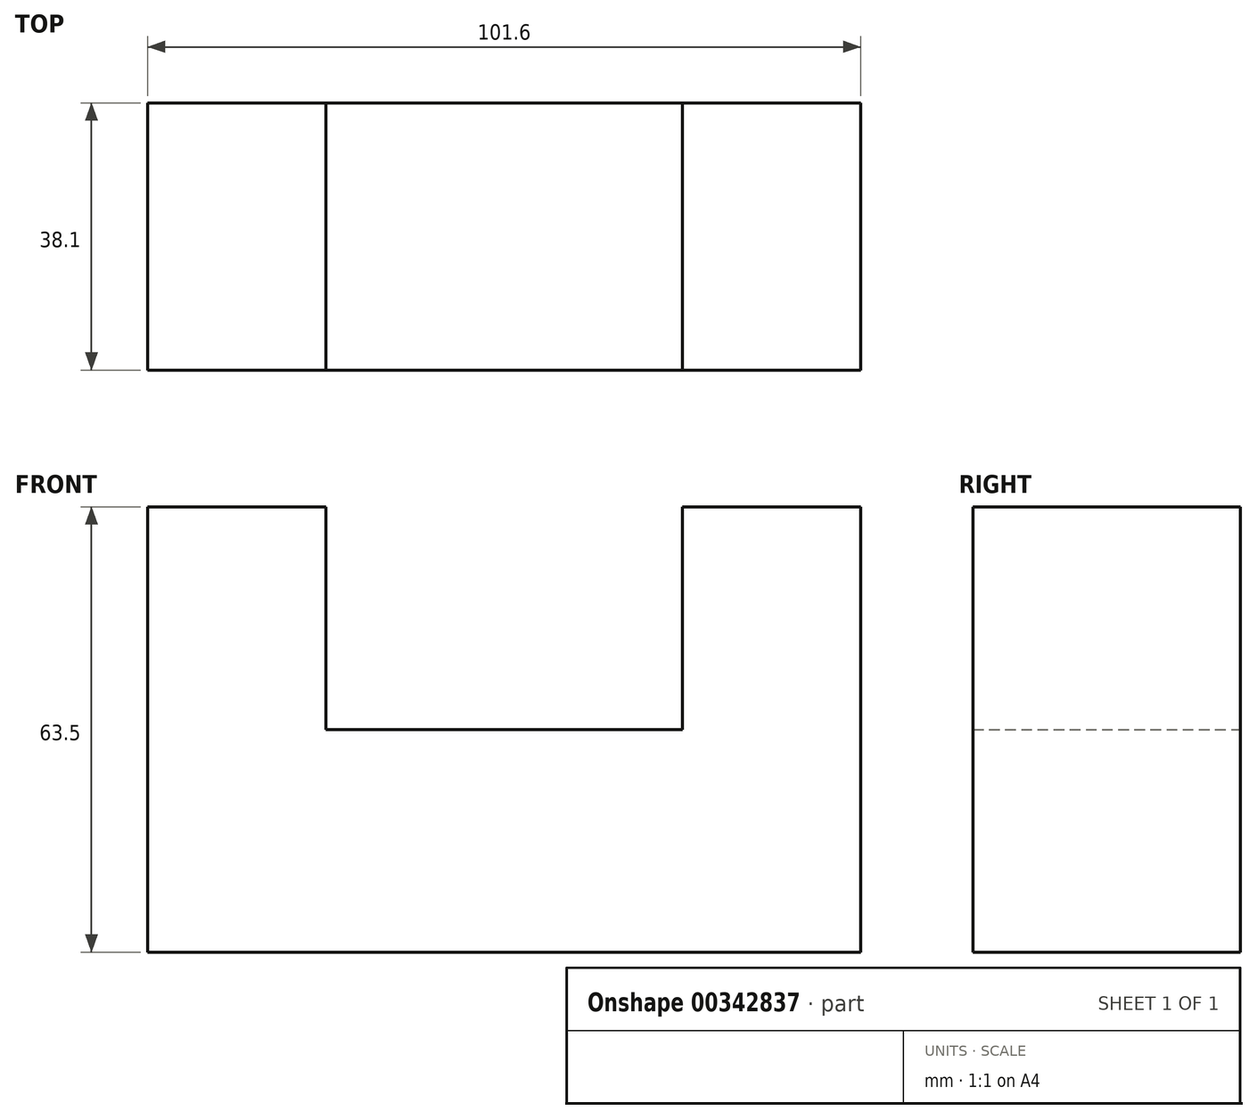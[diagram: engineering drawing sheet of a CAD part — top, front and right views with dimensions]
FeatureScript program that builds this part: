
annotation { "Feature Type Name" : "Feature", "Feature Type Description" : "" }
export const myFeature = defineFeature(function(context is Context, id is Id, definition is map)
    precondition{}
    {
        {
            var Q0;
            Q0=qCreatedBy(makeId("Front.planeOp"),FACE);
            var sketch = newSketch(context, id + "F0", { "sketchPlane" : qUnion([Q0])});
            skLineSegment(sketch, "E0", {"start": v(-23.03, -39.5) * mm, "end": v(78.57, -39.5) * mm});
            skLineSegment(sketch, "E1", {"start": v(78.57, -39.5) * mm, "end": v(78.57, 24) * mm});
            skLineSegment(sketch, "E2", {"start": v(78.57, 24) * mm, "end": v(53.17, 24) * mm});
            skLineSegment(sketch, "E3", {"start": v(53.17, 24) * mm, "end": v(53.17, -7.74) * mm});
            skLineSegment(sketch, "E4", {"start": v(53.17, -7.74) * mm, "end": v(2.37, -7.74) * mm});
            skLineSegment(sketch, "E5", {"start": v(2.37, -7.74) * mm, "end": v(2.37, 24) * mm});
            skLineSegment(sketch, "E6", {"start": v(2.37, 24) * mm, "end": v(-23.03, 24) * mm});
            skLineSegment(sketch, "E7", {"start": v(-23.03, 24) * mm, "end": v(-23.03, -39.5) * mm});
            skSolve(sketch);
        }
        {
            var Q0;
            Q0=makeQuery(id+"F0.imprint","IMPRINT",FACE,{"disambiguationData":[TD([[makeQuery(id+"F0.imprint","IMPRINT",EDGE,{"derivedFrom":sQuery(id+"F0.wireOp",EDGE,"E0")}),1.0]])]});
            extrude(context, id + "F1", {"entities" : qUnion([Q0]), "depth" : 38.1 * mm});
        }
    });
